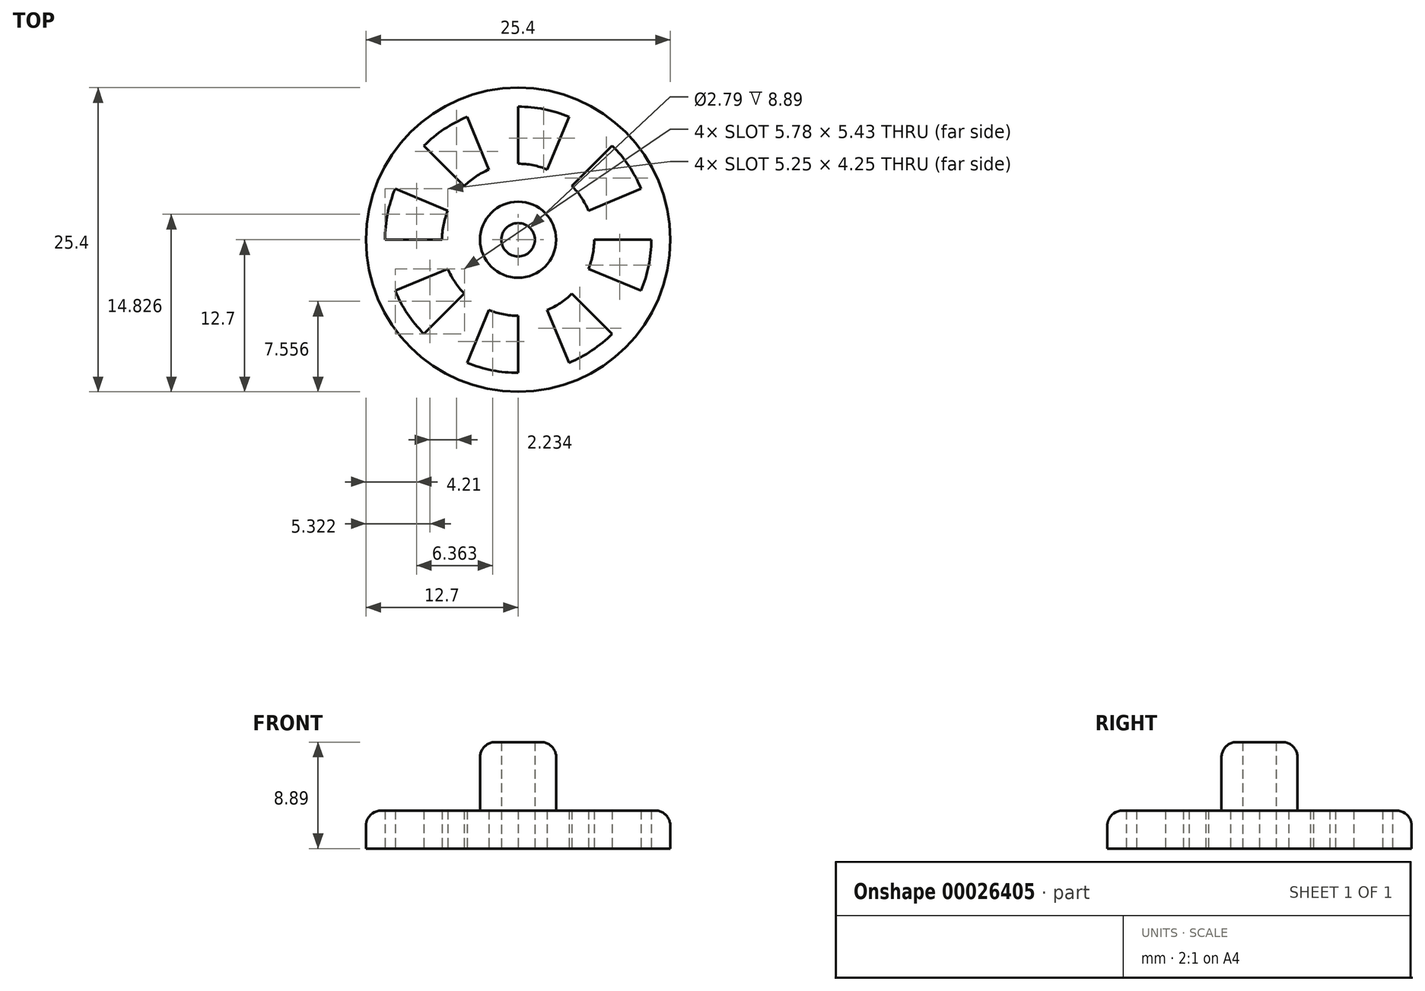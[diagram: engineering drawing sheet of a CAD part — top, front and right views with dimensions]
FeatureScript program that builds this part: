
annotation { "Feature Type Name" : "Feature", "Feature Type Description" : "" }
export const myFeature = defineFeature(function(context is Context, id is Id, definition is map)
    precondition{}
    {
        {
            var Q0;
            Q0=qCreatedBy(makeId("Top.planeOp"),FACE);
            var sketch = newSketch(context, id + "F0", { "sketchPlane" : qUnion([Q0])});
            skCircle(sketch, "E0", {"center": v(0, 0) * mm, "radius": 12.7 * mm});
            skSolve(sketch);
        }
        {
            var Q0;
            Q0 = qSketchRegion(id + "F0", true);
            extrude(context, id + "F1", {"entities" : qUnion([Q0]), "depth" : 3.17 * mm});
        }
        {
            var Q0;
            Q0=makeQuery(id+"F1.opExtrude","CAP_FACE",FACE,{"disambiguationData":[OSD([sQuery(id+"F0.wireOp",EDGE,"E0")])],"isStart":false});
            var sketch = newSketch(context, id + "F2", { "sketchPlane" : qUnion([Q0])});
            skCircle(sketch, "E1", {"center": v(0, 0) * mm, "radius": 3.18 * mm});
            skSolve(sketch);
        }
        {
            var Q0;
            Q0 = qSketchRegion(id + "F2", true);
            extrude(context, id + "F3", {"entities" : qUnion([Q0]), "operationType" : NewBodyOperationType.ADD, "depth" : 5.7 * mm});
        }
        {
            var Q0;
            Q0=makeQuery(id+"F1.opExtrude","CAP_FACE",FACE,{"disambiguationData":[OSD([sQuery(id+"F0.wireOp",EDGE,"E0")])],"isStart":true});
            var sketch = newSketch(context, id + "F4", { "sketchPlane" : qUnion([Q0])});
            skCircle(sketch, "E2", {"center": v(0, 0) * mm, "radius": 0.95 * mm});
            skSolve(sketch);
        }
        {
            var Q0;
            Q0 = qSketchRegion(id + "F4", true);
            extrude(context, id + "F5", {"entities" : qUnion([Q0]), "operationType" : NewBodyOperationType.REMOVE, "oppositeDirection" : true, "depth" : 25.4 * mm});
        }
        {
            var Q0;
            Q0=makeQuery(id+"F1.opExtrude","CAP_FACE",FACE,{"disambiguationData":[OSD([sQuery(id+"F0.wireOp",EDGE,"E0")])],"isStart":true});
            var sketch = newSketch(context, id + "F6", { "sketchPlane" : qUnion([Q0])});
            skCircle(sketch, "E3.0", {"center": v(0, 0) * mm, "radius": 12.7 * mm, "construction": true});
            skCircle(sketch, "E4.0", {"center": v(0, 0) * mm, "radius": 3.18 * mm, "construction": true});
            skCircle(sketch, "E5", {"center": v(0, 0) * mm, "radius": 11.11 * mm});
            skCircle(sketch, "E6", {"center": v(0, 0) * mm, "radius": 6.35 * mm});
            skSolve(sketch);
        }
        {
            var Q0;
            Q0=makeQuery(id+"F6.imprint","IMPRINT",FACE,{"disambiguationData":[TD([[makeQuery(id+"F6.imprint","IMPRINT",EDGE,{"derivedFrom":sQuery(id+"F6.wireOp",EDGE,"E5")}),1.0]])]});
            extrude(context, id + "F7", {"entities" : qUnion([Q0]), "operationType" : NewBodyOperationType.REMOVE, "oppositeDirection" : true, "depth" : 25.4 * mm});
        }
        {
            var Q0;
            Q0=makeQuery(id+"F7.boolean.opBoolean","SPLIT",FACE,{"disambiguationData":[TD([makeQuery(id+"F5.boolean.opBoolean","COPY",FACE,{"derivedFrom":makeQuery(id+"F5.opExtrude","SWEPT_FACE",FACE,{"disambiguationData":[OSD([sQuery(id+"F4.wireOp",EDGE,"E2")])]})})])],"derivedFrom":makeQuery(id+"F1.opExtrude","CAP_FACE",FACE,{"disambiguationData":[OSD([sQuery(id+"F0.wireOp",EDGE,"E0")])],"isStart":true})});
            var sketch = newSketch(context, id + "F8", { "sketchPlane" : qUnion([Q0])});
            skCircle(sketch, "E7.0.0", {"center": v(0, 0) * mm, "radius": 6.35 * mm, "construction": true});
            skCircle(sketch, "E8.0.0", {"center": v(0, 0) * mm, "radius": 12.7 * mm, "construction": true});
            skLineSegment(sketch, "E9", {"start": v(0, 0) * mm, "end": v(0, 12.7) * mm, "construction": true});
            skLineSegment(sketch, "E10", {"start": v(0, 12.7) * mm, "end": v(-12.7, 0) * mm, "construction": true});
            skLineSegment(sketch, "E11", {"start": v(-12.7, 0) * mm, "end": v(0, 0) * mm});
            skLineSegment(sketch, "E12", {"start": v(0, 0) * mm, "end": v(-6.35, 6.35) * mm, "construction": true});
            skLineSegment(sketch, "E13", {"start": v(-6.35, 6.35) * mm, "end": v(-8.98, 8.98) * mm, "construction": true});
            skLineSegment(sketch, "E14", {"start": v(-8.98, 8.98) * mm, "end": v(-12.7, 0) * mm, "construction": true});
            skLineSegment(sketch, "E15", {"start": v(0, 0) * mm, "end": v(-10.84, 4.5) * mm});
            skLineSegment(sketch, "E16", {"start": v(-10.84, 4.5) * mm, "end": v(-11.73, 4.86) * mm});
            skLineSegment(sketch, "E17", {"start": v(-11.73, 4.86) * mm, "end": v(-12.7, 0) * mm});
            skLineSegment(sketch, "E18.1.0", {"start": v(0, 0) * mm, "end": v(-10.84, -4.5) * mm});
            skLineSegment(sketch, "E18.1.1", {"start": v(-10.84, -4.5) * mm, "end": v(-11.73, -4.86) * mm});
            skLineSegment(sketch, "E18.1.2", {"start": v(-11.73, -4.86) * mm, "end": v(-8.98, -8.98) * mm});
            skLineSegment(sketch, "E18.1.3", {"start": v(-8.98, -8.98) * mm, "end": v(0, 0) * mm});
            skLineSegment(sketch, "E18.2.0", {"start": v(0, 0) * mm, "end": v(-4.5, -10.84) * mm});
            skLineSegment(sketch, "E18.2.1", {"start": v(-4.5, -10.84) * mm, "end": v(-4.86, -11.73) * mm});
            skLineSegment(sketch, "E18.2.2", {"start": v(-4.86, -11.73) * mm, "end": v(0, -12.7) * mm});
            skLineSegment(sketch, "E18.2.3", {"start": v(0, -12.7) * mm, "end": v(0, 0) * mm});
            skLineSegment(sketch, "E18.3.0", {"start": v(0, 0) * mm, "end": v(4.5, -10.84) * mm});
            skLineSegment(sketch, "E18.3.1", {"start": v(4.5, -10.84) * mm, "end": v(4.86, -11.73) * mm});
            skLineSegment(sketch, "E18.3.2", {"start": v(4.86, -11.73) * mm, "end": v(8.98, -8.98) * mm});
            skLineSegment(sketch, "E18.3.3", {"start": v(8.98, -8.98) * mm, "end": v(0, 0) * mm});
            skLineSegment(sketch, "E18.4.0", {"start": v(0, 0) * mm, "end": v(10.84, -4.5) * mm});
            skLineSegment(sketch, "E18.4.1", {"start": v(10.84, -4.5) * mm, "end": v(11.73, -4.86) * mm});
            skLineSegment(sketch, "E18.4.2", {"start": v(11.73, -4.86) * mm, "end": v(12.7, 0) * mm});
            skLineSegment(sketch, "E18.4.3", {"start": v(12.7, 0) * mm, "end": v(0, 0) * mm});
            skLineSegment(sketch, "E18.5.0", {"start": v(0, 0) * mm, "end": v(10.84, 4.5) * mm});
            skLineSegment(sketch, "E18.5.1", {"start": v(10.84, 4.5) * mm, "end": v(11.73, 4.86) * mm});
            skLineSegment(sketch, "E18.5.2", {"start": v(11.73, 4.86) * mm, "end": v(8.98, 8.98) * mm});
            skLineSegment(sketch, "E18.5.3", {"start": v(8.98, 8.98) * mm, "end": v(0, 0) * mm});
            skLineSegment(sketch, "E18.6.0", {"start": v(0, 0) * mm, "end": v(4.5, 10.84) * mm});
            skLineSegment(sketch, "E18.6.1", {"start": v(4.5, 10.84) * mm, "end": v(4.86, 11.73) * mm});
            skLineSegment(sketch, "E18.6.2", {"start": v(4.86, 11.73) * mm, "end": v(0, 12.7) * mm});
            skLineSegment(sketch, "E18.6.3", {"start": v(0, 12.7) * mm, "end": v(0, 0) * mm});
            skLineSegment(sketch, "E18.7.0", {"start": v(0, 0) * mm, "end": v(-4.5, 10.84) * mm});
            skLineSegment(sketch, "E18.7.1", {"start": v(-4.5, 10.84) * mm, "end": v(-4.86, 11.73) * mm});
            skLineSegment(sketch, "E18.7.2", {"start": v(-4.86, 11.73) * mm, "end": v(-8.98, 8.98) * mm});
            skLineSegment(sketch, "E18.7.3", {"start": v(-8.98, 8.98) * mm, "end": v(0, 0) * mm});
            skSolve(sketch);
        }
        {
            var Q0;
            {var subQ4=sQuery(id+"F8.wireOp",EDGE,"E18.7.1");Q0=makeQuery(id+"F8.imprint","IMPRINT",FACE,{"disambiguationData":[TD([[makeQuery(id+"F8.imprint","IMPRINT",EDGE,{"derivedFrom":subQ4}),1.0]])]});}
            var Q1;
            {var subQ1=sQuery(id+"F8.wireOp",EDGE,"E16");Q1=makeQuery(id+"F8.imprint","IMPRINT",FACE,{"disambiguationData":[TD([[makeQuery(id+"F8.imprint","IMPRINT",EDGE,{"derivedFrom":subQ1}),1.0]])]});}
            var Q2;
            {var subQ4=sQuery(id+"F8.wireOp",EDGE,"E18.1.1");Q2=makeQuery(id+"F8.imprint","IMPRINT",FACE,{"disambiguationData":[TD([[makeQuery(id+"F8.imprint","IMPRINT",EDGE,{"derivedFrom":subQ4}),1.0]])]});}
            var Q3;
            {var subQ4=sQuery(id+"F8.wireOp",EDGE,"E18.2.1");Q3=makeQuery(id+"F8.imprint","IMPRINT",FACE,{"disambiguationData":[TD([[makeQuery(id+"F8.imprint","IMPRINT",EDGE,{"derivedFrom":subQ4}),1.0]])]});}
            var Q4;
            {var subQ4=sQuery(id+"F8.wireOp",EDGE,"E18.3.1");Q4=makeQuery(id+"F8.imprint","IMPRINT",FACE,{"disambiguationData":[TD([[makeQuery(id+"F8.imprint","IMPRINT",EDGE,{"derivedFrom":subQ4}),1.0]])]});}
            var Q5;
            {var subQ4=sQuery(id+"F8.wireOp",EDGE,"E18.5.1");Q5=makeQuery(id+"F8.imprint","IMPRINT",FACE,{"disambiguationData":[TD([[makeQuery(id+"F8.imprint","IMPRINT",EDGE,{"derivedFrom":subQ4}),1.0]])]});}
            var Q6;
            {var subQ6=sQuery(id+"F8.wireOp",EDGE,"E18.6.1");Q6=makeQuery(id+"F8.imprint","IMPRINT",FACE,{"disambiguationData":[TD([[makeQuery(id+"F8.imprint","IMPRINT",EDGE,{"derivedFrom":subQ6}),1.0]])]});}
            var Q7;
            {var subQ6=sQuery(id+"F8.wireOp",EDGE,"E18.4.1");Q7=makeQuery(id+"F8.imprint","IMPRINT",FACE,{"disambiguationData":[TD([[makeQuery(id+"F8.imprint","IMPRINT",EDGE,{"derivedFrom":subQ6}),1.0]])]});}
            var Q8;
            Q8=makeQuery(id+"F7.boolean.opBoolean","SPLIT",FACE,{"disambiguationData":[TD([makeQuery(id+"F3.opExtrude","SWEPT_FACE",FACE,{"disambiguationData":[OSD([sQuery(id+"F2.wireOp",EDGE,"E1")])]})])],"derivedFrom":makeQuery(id+"F1.opExtrude","CAP_FACE",FACE,{"disambiguationData":[OSD([sQuery(id+"F0.wireOp",EDGE,"E0")])],"isStart":false})});
            extrude(context, id + "F9", {"entities" : qUnion([Q0, Q1, Q2, Q3, Q4, Q5, Q6, Q7]), "operationType" : NewBodyOperationType.ADD, "endBound" : BoundingType.UP_TO_SURFACE, "oppositeDirection" : true, "endBoundEntityFace" : qUnion([Q8]), "depth" : 25.4 * mm});
        }
        {
            var Q0;
            Q0=makeQuery(id+"F3.opExtrude","CAP_EDGE",EDGE,{"disambiguationData":[OSD([sQuery(id+"F2.wireOp",EDGE,"E1")])],"isStart":false});
            var Q1;
            Q1=makeQuery(id+"F3.opExtrude","CAP_EDGE",EDGE,{"disambiguationData":[OSD([sQuery(id+"F2.wireOp",EDGE,"E1")])],"isStart":true});
            var Q2;
            Q2=makeQuery(id+"F1.opExtrude","CAP_EDGE",EDGE,{"disambiguationData":[OSD([sQuery(id+"F0.wireOp",EDGE,"E0")])],"isStart":false});
            fillet(context, id + "F10", {"entities" : qUnion([Q0, Q1, Q2]), "radius" : 1.27 * mm, "tangentPropagation" : true, "allowEdgeOverflow" : false});
        }
        {
            var Q0;
            {var subQ0=sQuery(id+"F6.wireOp",EDGE,"E6");var subQ1=sQuery(id+"F0.wireOp",EDGE,"E0");var subQ2=makeQuery(id+"F1.opExtrude","CAP_FACE",FACE,{"disambiguationData":[OSD([subQ1])],"isStart":true});Q0=makeQuery(id+"F9.boolean.opBoolean","MERGE",FACE,{"derivedFrom":[makeQuery(id+"F7.boolean.opBoolean","SPLIT",FACE,{"disambiguationData":[TD([makeQuery(id+"F1.opExtrude","SWEPT_FACE",FACE,{"disambiguationData":[OSD([subQ1])]})])],"derivedFrom":subQ2}),makeQuery(id+"F7.boolean.opBoolean","SPLIT",FACE,{"disambiguationData":[TD([makeQuery(id+"F5.boolean.opBoolean","COPY",FACE,{"derivedFrom":makeQuery(id+"F5.opExtrude","SWEPT_FACE",FACE,{"disambiguationData":[OSD([sQuery(id+"F4.wireOp",EDGE,"E2")])]})})])],"derivedFrom":subQ2}),makeQuery(id+"F9.opExtrude","CAP_FACE",FACE,{"disambiguationData":[OSD([subQ0,sQuery(id+"F8.wireOp",EDGE,"E11"),sQuery(id+"F8.wireOp",EDGE,"E15"),sQuery(id+"F8.wireOp",EDGE,"E16"),sQuery(id+"F8.wireOp",EDGE,"E17")])],"isStart":true}),makeQuery(id+"F9.opExtrude","CAP_FACE",FACE,{"disambiguationData":[OSD([subQ0,sQuery(id+"F8.wireOp",EDGE,"E18.1.0"),sQuery(id+"F8.wireOp",EDGE,"E18.1.1"),sQuery(id+"F8.wireOp",EDGE,"E18.1.2"),sQuery(id+"F8.wireOp",EDGE,"E18.1.3")])],"isStart":true}),makeQuery(id+"F9.opExtrude","CAP_FACE",FACE,{"disambiguationData":[OSD([subQ0,sQuery(id+"F8.wireOp",EDGE,"E18.2.0"),sQuery(id+"F8.wireOp",EDGE,"E18.2.1"),sQuery(id+"F8.wireOp",EDGE,"E18.2.2"),sQuery(id+"F8.wireOp",EDGE,"E18.2.3")])],"isStart":true}),makeQuery(id+"F9.opExtrude","CAP_FACE",FACE,{"disambiguationData":[OSD([subQ0,sQuery(id+"F8.wireOp",EDGE,"E18.3.0"),sQuery(id+"F8.wireOp",EDGE,"E18.3.1"),sQuery(id+"F8.wireOp",EDGE,"E18.3.2"),sQuery(id+"F8.wireOp",EDGE,"E18.3.3")])],"isStart":true}),makeQuery(id+"F9.opExtrude","CAP_FACE",FACE,{"disambiguationData":[OSD([subQ0,sQuery(id+"F8.wireOp",EDGE,"E18.4.0"),sQuery(id+"F8.wireOp",EDGE,"E18.4.1"),sQuery(id+"F8.wireOp",EDGE,"E18.4.2"),sQuery(id+"F8.wireOp",EDGE,"E18.4.3")])],"isStart":true}),makeQuery(id+"F9.opExtrude","CAP_FACE",FACE,{"disambiguationData":[OSD([subQ0,sQuery(id+"F8.wireOp",EDGE,"E18.5.0"),sQuery(id+"F8.wireOp",EDGE,"E18.5.1"),sQuery(id+"F8.wireOp",EDGE,"E18.5.2"),sQuery(id+"F8.wireOp",EDGE,"E18.5.3")])],"isStart":true}),makeQuery(id+"F9.opExtrude","CAP_FACE",FACE,{"disambiguationData":[OSD([subQ0,sQuery(id+"F8.wireOp",EDGE,"E18.6.0"),sQuery(id+"F8.wireOp",EDGE,"E18.6.1"),sQuery(id+"F8.wireOp",EDGE,"E18.6.2"),sQuery(id+"F8.wireOp",EDGE,"E18.6.3")])],"isStart":true}),makeQuery(id+"F9.opExtrude","CAP_FACE",FACE,{"disambiguationData":[OSD([subQ0,sQuery(id+"F8.wireOp",EDGE,"E18.7.0"),sQuery(id+"F8.wireOp",EDGE,"E18.7.1"),sQuery(id+"F8.wireOp",EDGE,"E18.7.2"),sQuery(id+"F8.wireOp",EDGE,"E18.7.3")])],"isStart":true})]});}
            var sketch = newSketch(context, id + "F11", { "sketchPlane" : qUnion([Q0])});
            skCircle(sketch, "E19", {"center": v(0, 0) * mm, "radius": 1.4 * mm});
            skSolve(sketch);
        }
        {
            var Q0;
            Q0 = qSketchRegion(id + "F11", true);
            extrude(context, id + "F12", {"entities" : qUnion([Q0]), "operationType" : NewBodyOperationType.REMOVE, "oppositeDirection" : true, "depth" : 25.4 * mm});
        }
    });
